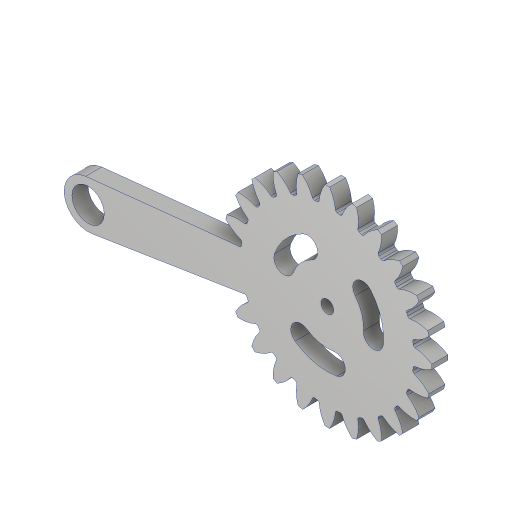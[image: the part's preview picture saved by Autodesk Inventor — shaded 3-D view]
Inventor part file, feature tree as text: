
AUTODESK INVENTOR PART (.ipt)
format: ipt  version: 2023.2 (Build 272271000, 271)  size: 772,096 bytes
history: native  units: mm
features: extrude x11, sketch x11, projected_geometry x6, fillet x3, other x1, pattern_circular x1
ambient origin geometry x8: Origin, YZ Plane, XZ Plane, XY Plane, X Axis, Y Axis, Z Axis, Center Point
bodies: Body1 (feature_tree)
feature tree (33):
  other  "솔리드1"
  extrude  "돌출1"  Depth=48.0mm
  pattern_circular  "원형 패턴1"  [2 undecoded]
  extrude  "돌출2"  Depth=43.0mm
  extrude  "돌출3"  Depth=1.57mm
  extrude  "돌출4"  Depth=1.0mm
  extrude  "돌출5"  Depth=0.5mm
  fillet  "모깎기1"  Radius=4.0mm
  fillet  "모깎기2"  Radius=240.0mm
  extrude  "돌출6"  Depth=7.0mm
  fillet  "모깎기3"  Radius=3.0mm
  extrude  "돌출9"  Depth=2.5mm
  extrude  "돌출10"  Depth=10.0mm TaperAngle=0.0deg
  extrude  "돌출11"  Depth=43.0mm
  extrude  "돌출7"  Depth=444.0mm TaperAngle=0.0deg
  extrude  "돌출8"  Depth=1.308997mm
  sketch  "스케치1"
  sketch  "스케치2"
  sketch  "스케치3"
  sketch  "스케치4"
  sketch  "스케치5"
  sketch  "스케치6"
  sketch  "스케치7"
  sketch  "스케치8"
  projected_geometry  "투영된 루프1"
  projected_geometry  "투영된 루프2"
  sketch  "스케치9"
  projected_geometry  "투영된 루프3"
  projected_geometry  "투영된 루프4"
  sketch  "스케치10"
  projected_geometry  "투영된 루프5"
  sketch  "스케치11"
  projected_geometry  "투영된 루프6"
note: 2 required parameter values undecoded (feature->parameter linkage not recoverable at this tier; creation-order binding heuristic only, values carry confidence <= 0.55)
